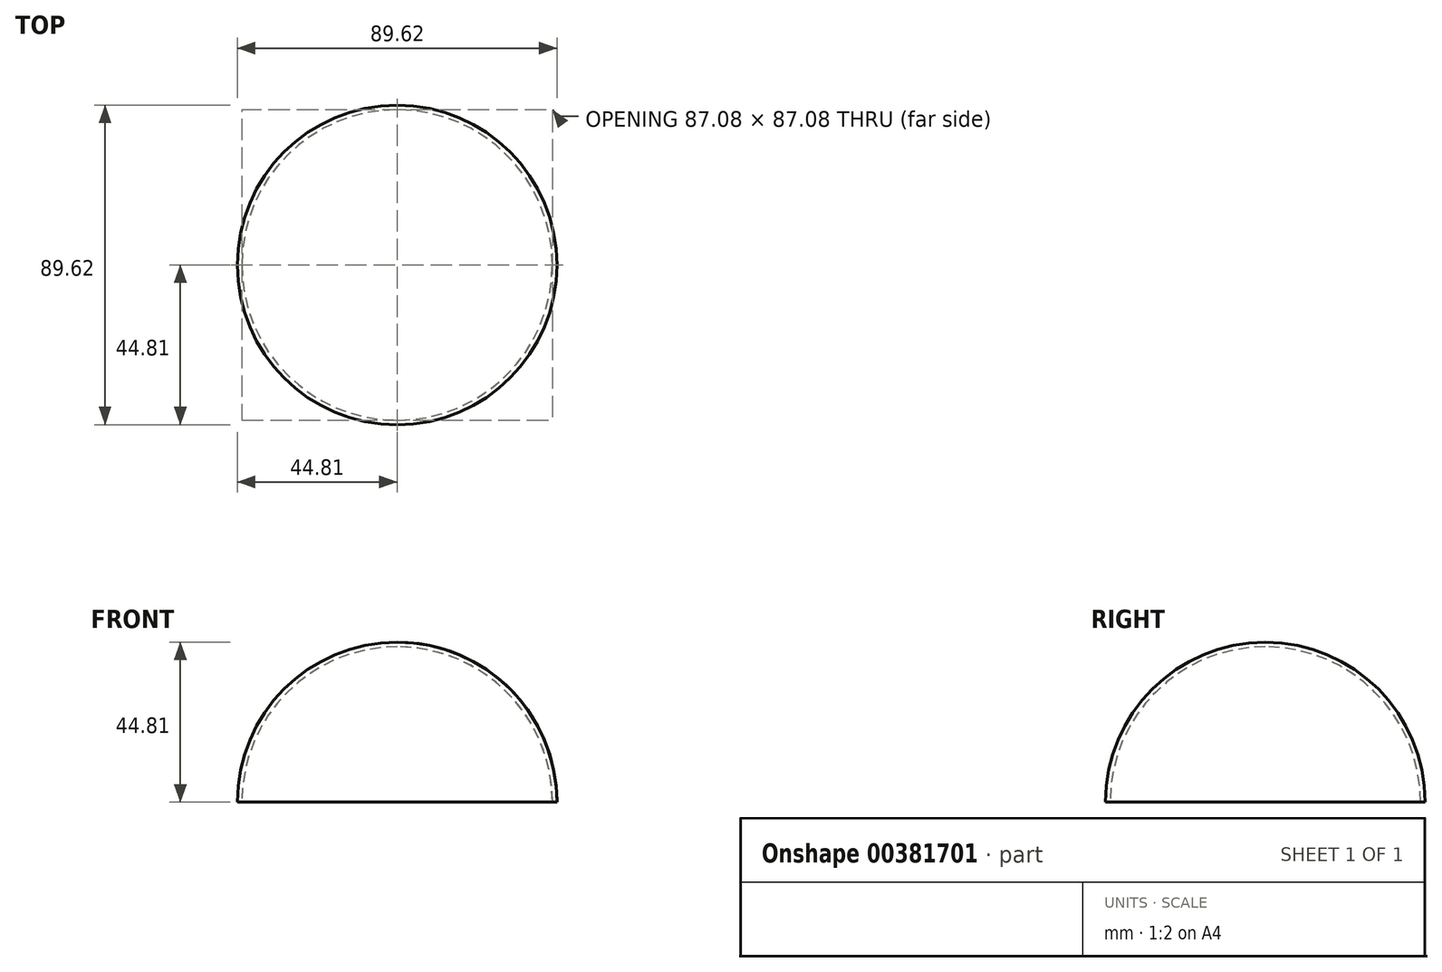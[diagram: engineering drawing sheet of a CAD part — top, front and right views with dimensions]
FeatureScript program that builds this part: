
annotation { "Feature Type Name" : "Feature", "Feature Type Description" : "" }
export const myFeature = defineFeature(function(context is Context, id is Id, definition is map)
    precondition{}
    {
        {
            var Q0;
            Q0=qCreatedBy(makeId("Front.planeOp"),FACE);
            var sketch = newSketch(context, id + "F0", { "sketchPlane" : qUnion([Q0])});
            skLineSegment(sketch, "E0", {"start": v(0, 58.86) * mm, "end": v(0, -56.01) * mm, "construction": true});
            skArc(sketch, "E1", {"start": v(-44.8, 0) * mm, "mid": v(-31.69, 31.69) * mm, "end": v(0, 44.8) * mm});
            skLineSegment(sketch, "E2", {"start": v(-44.8, 0) * mm, "end": v(0, 0) * mm});
            skLineSegment(sketch, "E3", {"start": v(0, 0) * mm, "end": v(0, 44.8) * mm});
            skSolve(sketch);
        }
        {
            var Q0;
            Q0 = qSketchRegion(id + "F0", true);
            var Q1;
            Q1=sQuery(id+"F0.wireOp",EDGE,"E0");
            revolve(context, id + "F1", {"entities" : qUnion([Q0]), "axis" : qUnion([Q1]), "revolveType" : RevolveType.FULL});
        }
        {
            var Q0;
            Q0=makeQuery(id+"F1.opRevolve","SWEPT_FACE",FACE,{"disambiguationData":[OSD([sQuery(id+"F0.wireOp",EDGE,"E2")])]});
            shell(context, id + "F2", {"entities" : qUnion([Q0]), "thickness" : 1.27 * mm});
        }
    });
